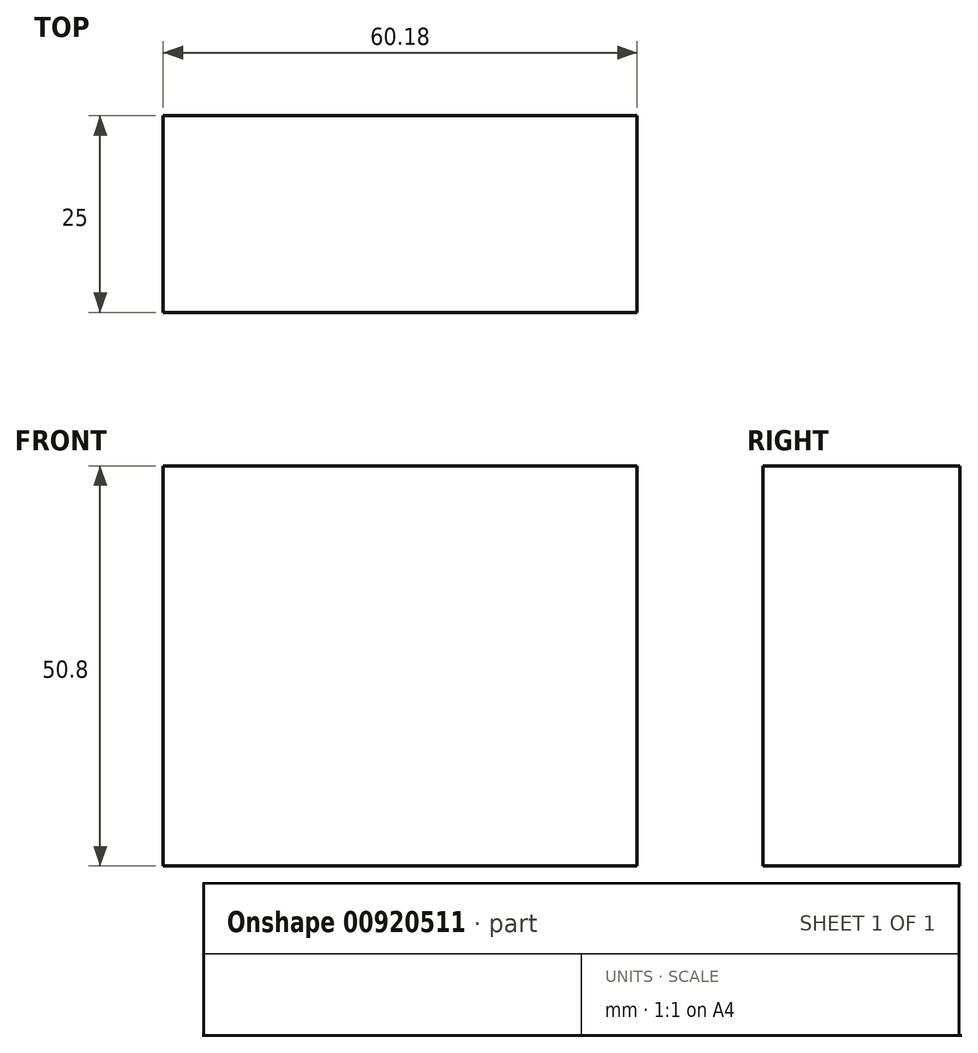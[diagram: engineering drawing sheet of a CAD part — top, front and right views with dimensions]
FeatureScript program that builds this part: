
annotation { "Feature Type Name" : "Feature", "Feature Type Description" : "" }
export const myFeature = defineFeature(function(context is Context, id is Id, definition is map)
    precondition{}
    {
        {
            var Q0;
            Q0=qCreatedBy(makeId("Front.planeOp"),FACE);
            var sketch = newSketch(context, id + "F0", { "sketchPlane" : qUnion([Q0])});
            skLineSegment(sketch, "E0.bottom", {"start": v(30.09, -25.4) * mm, "end": v(-30.09, -25.4) * mm});
            skLineSegment(sketch, "E0.top", {"start": v(30.09, 25.4) * mm, "end": v(-30.09, 25.4) * mm});
            skLineSegment(sketch, "E0.left", {"start": v(30.09, -25.4) * mm, "end": v(30.09, 25.4) * mm});
            skLineSegment(sketch, "E0.right", {"start": v(-30.09, -25.4) * mm, "end": v(-30.09, 25.4) * mm});
            skPoint(sketch, "E0.middle", {"position": v(0, 0) * mm});
            skSolve(sketch);
        }
        {
            var Q0;
            Q0=makeQuery(id+"F0.imprint","IMPRINT",FACE,{"disambiguationData":[TD([[makeQuery(id+"F0.imprint","IMPRINT",EDGE,{"derivedFrom":sQuery(id+"F0.wireOp",EDGE,"E0.bottom")}),-1.0]])]});
            extrude(context, id + "F1", {"entities" : qUnion([Q0]), "depth" : 25 * mm, "offsetDistance" : 25 * mm});
        }
    });
